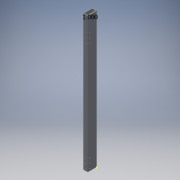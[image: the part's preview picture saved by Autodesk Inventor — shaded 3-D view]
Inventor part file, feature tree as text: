
AUTODESK INVENTOR PART (.ipt)
format: ipt  version: 2018 (Build 220112000, 112)  size: 176,128 bytes
history: native  units: in
note: dims shown in document units (in); Inventor stores cm internally (conversion verified against a paired STEP export)
features: sketch x5, extrude x4
ambient origin geometry x8: Origin, YZ Plane, XZ Plane, XY Plane, X Axis, Y Axis, Z Axis, Center Point
bodies: Solid1 (feature_tree)
feature tree (9):
  extrude  "Extrusion1"  Depth=2.0in
  extrude  "Extrusion3"  Depth=30.0in TaperAngle=0.0deg
  sketch  "Sketch4"  dims[d19=0.5in d20=1.0in]
  extrude  "Extrusion4"  Depth=1.0in
  extrude  "Extrusion5"  Depth=1.0in
  sketch  "Sketch1"  dims[d0=1.0in d1=2.0in]
  sketch  "Sketch3"  dims[d2=0.125in d3=30.0in d4=0.0in]
  sketch  "Sketch5"  dims[d21=1.0in d22=0.2031in]
  sketch  "Sketch6"  dims[d23=0.2031in d24=0.2031in d30=30.0in d31=0.0in d38=0.5in d39=0.2031in d40=1.0in d41=1.0in d42=0.2031in d43=0.2031in d44=1.0in d46=0.5in d47=0.5in d48=0.2031in d49=0.2031in d50=0.2031in d51=0.5in d52=0.5in d53=0.5in d54=0.2031in d55=0.2031in d56=0.2031in d57=30.0in d58=0.0in d59=1.0in d60=1.125in d61=12.0in d62=0.0in]
